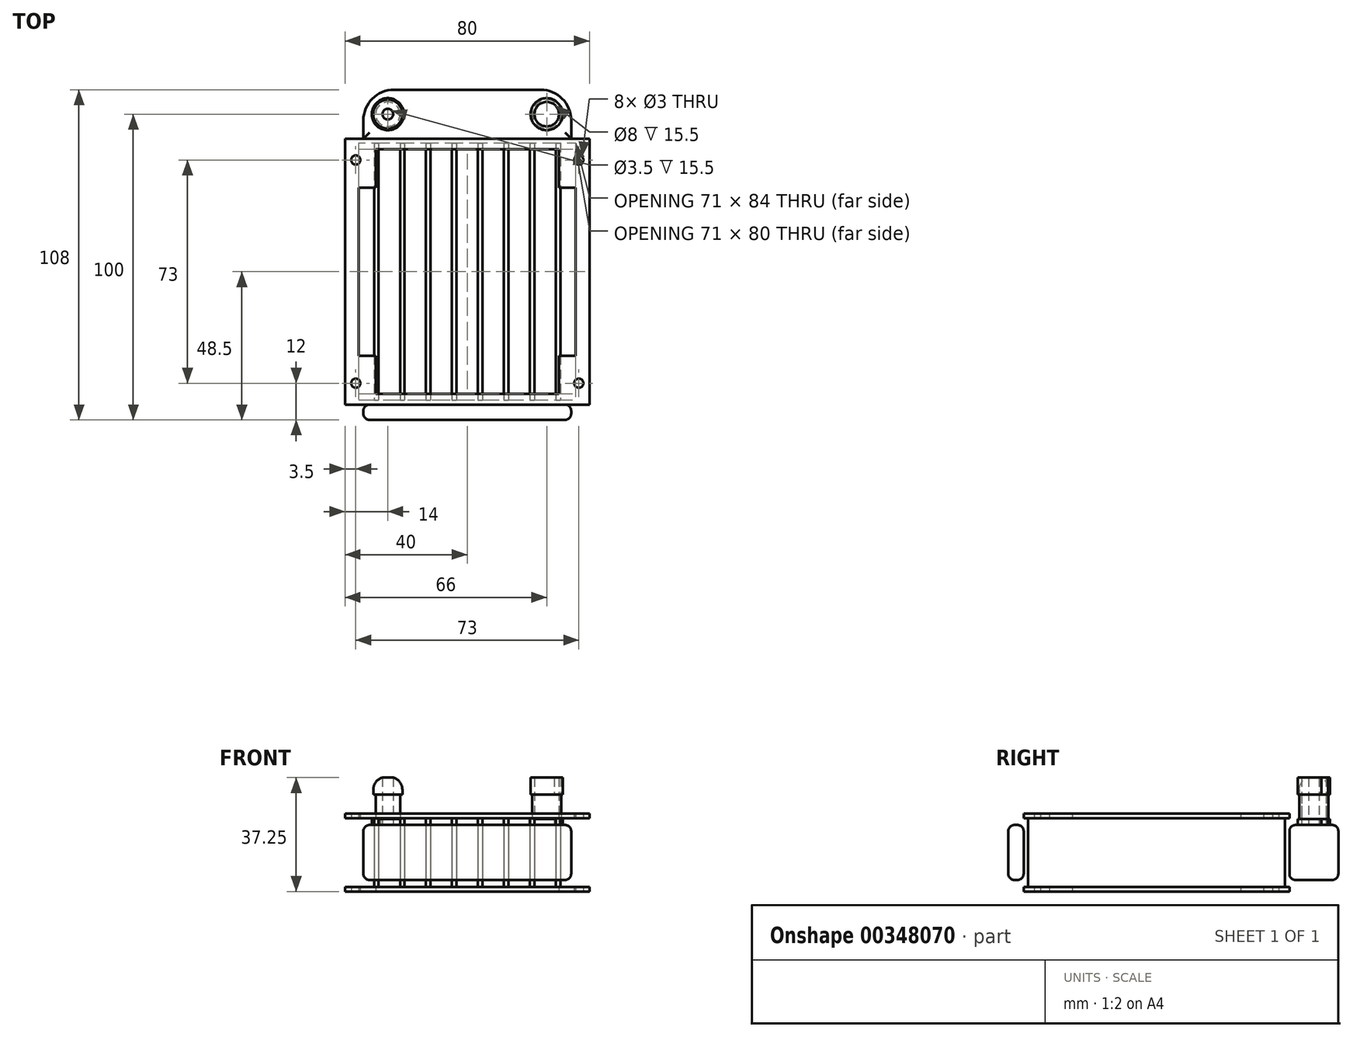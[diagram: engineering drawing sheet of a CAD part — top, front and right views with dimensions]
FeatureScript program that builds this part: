
annotation { "Feature Type Name" : "Feature", "Feature Type Description" : "" }
export const myFeature = defineFeature(function(context is Context, id is Id, definition is map)
    precondition{}
    {
        {
            var Q0;
            Q0=qCreatedBy(makeId("Top.planeOp"),FACE);
            var sketch = newSketch(context, id + "F0", { "sketchPlane" : qUnion([Q0])});
            skLineSegment(sketch, "E0.bottom", {"start": v(-40, 43.5) * mm, "end": v(40, 43.5) * mm});
            skLineSegment(sketch, "E0.top", {"start": v(-40, -43.5) * mm, "end": v(40, -43.5) * mm});
            skLineSegment(sketch, "E0.left", {"start": v(-40, 43.5) * mm, "end": v(-40, -43.5) * mm});
            skLineSegment(sketch, "E0.right", {"start": v(40, 43.5) * mm, "end": v(40, -43.5) * mm});
            skPoint(sketch, "E0.middle", {"position": v(0, 0) * mm});
            skLineSegment(sketch, "E1.bottom", {"start": v(40, 43.5) * mm, "end": v(30, 43.5) * mm});
            skLineSegment(sketch, "E1.top", {"start": v(35.5, 27.5) * mm, "end": v(30, 27.5) * mm});
            skLineSegment(sketch, "E1.left", {"start": v(40, 43.5) * mm, "end": v(40, 27.5) * mm});
            skLineSegment(sketch, "E1.right", {"start": v(30, 40) * mm, "end": v(30, 27.5) * mm});
            skCircle(sketch, "E2", {"center": v(36.5, 36.5) * mm, "radius": 1.5 * mm});
            skLineSegment(sketch, "E3.MirrorCS", {"start": v(-35.5, 27.5) * mm, "end": v(-30, 27.5) * mm});
            skLineSegment(sketch, "E4.MirrorCS", {"start": v(-30, 40) * mm, "end": v(-30, 27.5) * mm});
            skCircle(sketch, "E5.MirrorC", {"center": v(-36.5, 36.5) * mm, "radius": 1.5 * mm});
            skLineSegment(sketch, "E6.MirrorCS", {"start": v(-35.5, -27.5) * mm, "end": v(-30, -27.5) * mm});
            skLineSegment(sketch, "E7.MirrorCS", {"start": v(-30, -40) * mm, "end": v(-30, -27.5) * mm});
            skLineSegment(sketch, "E8.MirrorCS", {"start": v(35.5, -27.5) * mm, "end": v(30, -27.5) * mm});
            skLineSegment(sketch, "E9.MirrorCS", {"start": v(30, -40) * mm, "end": v(30, -27.5) * mm});
            skCircle(sketch, "E10.MirrorC", {"center": v(36.5, -36.5) * mm, "radius": 1.5 * mm});
            skCircle(sketch, "E11.MirrorC", {"center": v(-36.5, -36.5) * mm, "radius": 1.5 * mm});
            skLineSegment(sketch, "E12", {"start": v(35.5, 27.5) * mm, "end": v(35.5, -27.5) * mm});
            skLineSegment(sketch, "E13.MirrorCS", {"start": v(-35.5, 27.5) * mm, "end": v(-35.5, -27.5) * mm});
            skLineSegment(sketch, "E14", {"start": v(-30, 40) * mm, "end": v(30, 40) * mm});
            skLineSegment(sketch, "E15.MirrorCS", {"start": v(-30, -40) * mm, "end": v(30, -40) * mm});
            skPoint(sketch, "E16.orphan", {"position": v(-40, 27.5) * mm});
            skPoint(sketch, "E17.orphan", {"position": v(-40, -27.5) * mm});
            skPoint(sketch, "E18.orphan", {"position": v(40, -27.5) * mm});
            skPoint(sketch, "E19.orphan", {"position": v(-30, -43.5) * mm});
            skPoint(sketch, "E20.orphan", {"position": v(30, -43.5) * mm});
            skPoint(sketch, "E21.orphan", {"position": v(-30, 43.5) * mm});
            skSolve(sketch);
        }
        {
            var Q0;
            Q0=makeQuery(id+"F0.imprint","IMPRINT",FACE,{"disambiguationData":[TD([[makeQuery(id+"F0.imprint","IMPRINT",EDGE,{"derivedFrom":sQuery(id+"F0.wireOp",EDGE,"E0.bottom")}),-1.0]])]});
            extrude(context, id + "F1", {"entities" : qUnion([Q0]), "depth" : 1.5 * mm});
        }
        {
            var Q0;
            Q0=makeQuery(id+"F1.opExtrude","CAP_FACE",FACE,{"disambiguationData":[OSD([sQuery(id+"F0.wireOp",EDGE,"E0.bottom"),sQuery(id+"F0.wireOp",EDGE,"E0.top"),sQuery(id+"F0.wireOp",EDGE,"E0.left"),sQuery(id+"F0.wireOp",EDGE,"E0.right"),sQuery(id+"F0.wireOp",EDGE,"E1.bottom"),sQuery(id+"F0.wireOp",EDGE,"E1.top"),sQuery(id+"F0.wireOp",EDGE,"E1.left"),sQuery(id+"F0.wireOp",EDGE,"E1.right"),sQuery(id+"F0.wireOp",EDGE,"E2"),sQuery(id+"F0.wireOp",EDGE,"E3.MirrorCS"),sQuery(id+"F0.wireOp",EDGE,"E4.MirrorCS"),sQuery(id+"F0.wireOp",EDGE,"E5.MirrorC"),sQuery(id+"F0.wireOp",EDGE,"E6.MirrorCS"),sQuery(id+"F0.wireOp",EDGE,"E7.MirrorCS"),sQuery(id+"F0.wireOp",EDGE,"E8.MirrorCS"),sQuery(id+"F0.wireOp",EDGE,"E9.MirrorCS"),sQuery(id+"F0.wireOp",EDGE,"E10.MirrorC"),sQuery(id+"F0.wireOp",EDGE,"E11.MirrorC"),sQuery(id+"F0.wireOp",EDGE,"E12"),sQuery(id+"F0.wireOp",EDGE,"E13.MirrorCS"),sQuery(id+"F0.wireOp",EDGE,"E14"),sQuery(id+"F0.wireOp",EDGE,"E15.MirrorCS")])],"isStart":false});
            var sketch = newSketch(context, id + "F2", { "sketchPlane" : qUnion([Q0])});
            skLineSegment(sketch, "E22.bottom", {"start": v(-40, 43.5) * mm, "end": v(40, 43.5) * mm});
            skLineSegment(sketch, "E22.top", {"start": v(-40, -43.5) * mm, "end": v(40, -43.5) * mm});
            skLineSegment(sketch, "E22.left", {"start": v(-40, 43.5) * mm, "end": v(-40, -43.5) * mm});
            skLineSegment(sketch, "E22.right", {"start": v(40, 43.5) * mm, "end": v(40, -43.5) * mm});
            skPoint(sketch, "E22.middle", {"position": v(0, 0) * mm});
            skLineSegment(sketch, "E23.bottom", {"start": v(-38.5, 42) * mm, "end": v(38.5, 42) * mm});
            skLineSegment(sketch, "E23.top", {"start": v(-38.5, -42) * mm, "end": v(38.5, -42) * mm});
            skLineSegment(sketch, "E23.left", {"start": v(-38.5, 42) * mm, "end": v(-38.5, -42) * mm});
            skLineSegment(sketch, "E23.right", {"start": v(38.5, 42) * mm, "end": v(38.5, -42) * mm});
            skLineSegment(sketch, "E24.left", {"start": v(-30.5, 42) * mm, "end": v(-30.5, -42) * mm});
            skLineSegment(sketch, "E24.right", {"start": v(-29, 42) * mm, "end": v(-29, -42) * mm});
            skLineSegment(sketch, "E25.1.0.0", {"start": v(-20.5, 42) * mm, "end": v(-20.5, -42) * mm});
            skLineSegment(sketch, "E25.1.0.1", {"start": v(-22, 42) * mm, "end": v(-22, -42) * mm});
            skLineSegment(sketch, "E25.2.0.0", {"start": v(-12, 42) * mm, "end": v(-12, -42) * mm});
            skLineSegment(sketch, "E25.2.0.1", {"start": v(-13.5, 42) * mm, "end": v(-13.5, -42) * mm});
            skLineSegment(sketch, "E25.3.0.0", {"start": v(-3.5, 42) * mm, "end": v(-3.5, -42) * mm});
            skLineSegment(sketch, "E25.3.0.1", {"start": v(-5, 42) * mm, "end": v(-5, -42) * mm});
            skLineSegment(sketch, "E25.4.0.0", {"start": v(5, 42) * mm, "end": v(5, -42) * mm});
            skLineSegment(sketch, "E25.4.0.1", {"start": v(3.5, 42) * mm, "end": v(3.5, -42) * mm});
            skLineSegment(sketch, "E25.5.0.0", {"start": v(13.5, 42) * mm, "end": v(13.5, -42) * mm});
            skLineSegment(sketch, "E25.5.0.1", {"start": v(12, 42) * mm, "end": v(12, -42) * mm});
            skLineSegment(sketch, "E25.6.0.0", {"start": v(22, 42) * mm, "end": v(22, -42) * mm});
            skLineSegment(sketch, "E25.6.0.1", {"start": v(20.5, 42) * mm, "end": v(20.5, -42) * mm});
            skLineSegment(sketch, "E25.7.0.0", {"start": v(30.5, 42) * mm, "end": v(30.5, -42) * mm});
            skLineSegment(sketch, "E25.7.0.1", {"start": v(29, 42) * mm, "end": v(29, -42) * mm});
            skSolve(sketch);
        }
        {
            var Q0;
            Q0=makeQuery(id+"F2.imprint","IMPRINT",FACE,{"disambiguationData":[TD([[makeQuery(id+"F2.imprint","IMPRINT",EDGE,{"derivedFrom":sQuery(id+"F2.wireOp",EDGE,"E22.bottom")}),1.0]])]});
            var Q1;
            {var subQ4=makeQuery(id+"F1.opExtrude","CAP_EDGE",EDGE,{"disambiguationData":[OSD([sQuery(id+"F0.wireOp",EDGE,"E4.MirrorCS")])],"isStart":false});Q1=makeQuery(id+"F2.imprint","IMPRINT",FACE,{"disambiguationData":[TD([[makeQuery(id+"F2.imprint","IMPRINT",EDGE,{"derivedFrom":subQ4}),1.0]])]});}
            var Q2;
            {var subQ5=makeQuery(id+"F1.opExtrude","CAP_EDGE",EDGE,{"disambiguationData":[OSD([sQuery(id+"F0.wireOp",EDGE,"E4.MirrorCS")])],"isStart":false});Q2=makeQuery(id+"F2.imprint","IMPRINT",FACE,{"disambiguationData":[TD([[makeQuery(id+"F2.imprint","IMPRINT",EDGE,{"derivedFrom":subQ5}),-1.0]])]});}
            var Q3;
            {var subQ0=sQuery(id+"F2.wireOp",EDGE,"E25.1.0.0");var subQ1=makeQuery(id+"F1.opExtrude","CAP_EDGE",EDGE,{"disambiguationData":[OSD([sQuery(id+"F0.wireOp",EDGE,"E14")])],"isStart":false});var subQ2=makeQuery(id+"F2.imprint","INTERSECT",VERTEX,{"derivedFrom":[subQ1,subQ0]});Q3=makeQuery(id+"F2.imprint","IMPRINT",FACE,{"disambiguationData":[TD([[makeQuery(id+"F2.imprint","IMPRINT",EDGE,{"disambiguationData":[TD([[subQ2,-1.0]])],"derivedFrom":subQ0}),-1.0]])]});}
            var Q4;
            {var subQ0=sQuery(id+"F2.wireOp",EDGE,"E25.2.0.0");var subQ1=makeQuery(id+"F1.opExtrude","CAP_EDGE",EDGE,{"disambiguationData":[OSD([sQuery(id+"F0.wireOp",EDGE,"E14")])],"isStart":false});var subQ2=makeQuery(id+"F2.imprint","INTERSECT",VERTEX,{"derivedFrom":[subQ1,subQ0]});Q4=makeQuery(id+"F2.imprint","IMPRINT",FACE,{"disambiguationData":[TD([[makeQuery(id+"F2.imprint","IMPRINT",EDGE,{"disambiguationData":[TD([[subQ2,-1.0]])],"derivedFrom":subQ0}),-1.0]])]});}
            var Q5;
            {var subQ0=sQuery(id+"F2.wireOp",EDGE,"E25.3.0.0");var subQ1=makeQuery(id+"F1.opExtrude","CAP_EDGE",EDGE,{"disambiguationData":[OSD([sQuery(id+"F0.wireOp",EDGE,"E14")])],"isStart":false});var subQ2=makeQuery(id+"F2.imprint","INTERSECT",VERTEX,{"derivedFrom":[subQ1,subQ0]});Q5=makeQuery(id+"F2.imprint","IMPRINT",FACE,{"disambiguationData":[TD([[makeQuery(id+"F2.imprint","IMPRINT",EDGE,{"disambiguationData":[TD([[subQ2,-1.0]])],"derivedFrom":subQ0}),-1.0]])]});}
            var Q6;
            {var subQ0=sQuery(id+"F2.wireOp",EDGE,"E25.4.0.0");var subQ1=makeQuery(id+"F1.opExtrude","CAP_EDGE",EDGE,{"disambiguationData":[OSD([sQuery(id+"F0.wireOp",EDGE,"E14")])],"isStart":false});var subQ2=makeQuery(id+"F2.imprint","INTERSECT",VERTEX,{"derivedFrom":[subQ1,subQ0]});Q6=makeQuery(id+"F2.imprint","IMPRINT",FACE,{"disambiguationData":[TD([[makeQuery(id+"F2.imprint","IMPRINT",EDGE,{"disambiguationData":[TD([[subQ2,-1.0]])],"derivedFrom":subQ0}),-1.0]])]});}
            var Q7;
            {var subQ0=sQuery(id+"F2.wireOp",EDGE,"E25.5.0.0");var subQ1=makeQuery(id+"F1.opExtrude","CAP_EDGE",EDGE,{"disambiguationData":[OSD([sQuery(id+"F0.wireOp",EDGE,"E14")])],"isStart":false});var subQ2=makeQuery(id+"F2.imprint","INTERSECT",VERTEX,{"derivedFrom":[subQ1,subQ0]});Q7=makeQuery(id+"F2.imprint","IMPRINT",FACE,{"disambiguationData":[TD([[makeQuery(id+"F2.imprint","IMPRINT",EDGE,{"disambiguationData":[TD([[subQ2,-1.0]])],"derivedFrom":subQ0}),-1.0]])]});}
            var Q8;
            {var subQ0=sQuery(id+"F2.wireOp",EDGE,"E25.6.0.0");var subQ1=makeQuery(id+"F1.opExtrude","CAP_EDGE",EDGE,{"disambiguationData":[OSD([sQuery(id+"F0.wireOp",EDGE,"E14")])],"isStart":false});var subQ2=makeQuery(id+"F2.imprint","INTERSECT",VERTEX,{"derivedFrom":[subQ1,subQ0]});Q8=makeQuery(id+"F2.imprint","IMPRINT",FACE,{"disambiguationData":[TD([[makeQuery(id+"F2.imprint","IMPRINT",EDGE,{"disambiguationData":[TD([[subQ2,-1.0]])],"derivedFrom":subQ0}),-1.0]])]});}
            var Q9;
            {var subQ6=makeQuery(id+"F1.opExtrude","CAP_EDGE",EDGE,{"disambiguationData":[OSD([sQuery(id+"F0.wireOp",EDGE,"E1.right")])],"isStart":false});Q9=makeQuery(id+"F2.imprint","IMPRINT",FACE,{"disambiguationData":[TD([[makeQuery(id+"F2.imprint","IMPRINT",EDGE,{"derivedFrom":subQ6}),-1.0]])]});}
            var Q10;
            {var subQ0=makeQuery(id+"F1.opExtrude","CAP_EDGE",EDGE,{"disambiguationData":[OSD([sQuery(id+"F0.wireOp",EDGE,"E9.MirrorCS")])],"isStart":false});Q10=makeQuery(id+"F2.imprint","IMPRINT",FACE,{"disambiguationData":[TD([[makeQuery(id+"F2.imprint","IMPRINT",EDGE,{"derivedFrom":subQ0}),-1.0]])]});}
            var Q11;
            {var subQ0=makeQuery(id+"F1.opExtrude","CAP_EDGE",EDGE,{"disambiguationData":[OSD([sQuery(id+"F0.wireOp",EDGE,"E1.right")])],"isStart":false});Q11=makeQuery(id+"F2.imprint","IMPRINT",FACE,{"disambiguationData":[TD([[makeQuery(id+"F2.imprint","IMPRINT",EDGE,{"derivedFrom":subQ0}),1.0]])]});}
            var Q12;
            {var subQ5=makeQuery(id+"F1.opExtrude","CAP_EDGE",EDGE,{"disambiguationData":[OSD([sQuery(id+"F0.wireOp",EDGE,"E7.MirrorCS")])],"isStart":false});Q12=makeQuery(id+"F2.imprint","IMPRINT",FACE,{"disambiguationData":[TD([[makeQuery(id+"F2.imprint","IMPRINT",EDGE,{"derivedFrom":subQ5}),1.0]])]});}
            var Q13;
            {var subQ0=sQuery(id+"F2.wireOp",EDGE,"E25.6.0.0");var subQ1=sQuery(id+"F2.wireOp",EDGE,"E23.top");var subQ2=makeQuery(id+"F2.imprint","INTERSECT",VERTEX,{"derivedFrom":[subQ1,subQ0]});Q13=makeQuery(id+"F2.imprint","IMPRINT",FACE,{"disambiguationData":[TD([[makeQuery(id+"F2.imprint","IMPRINT",EDGE,{"disambiguationData":[TD([[subQ2,1.0]])],"derivedFrom":subQ1}),1.0]])]});}
            var Q14;
            {var subQ0=sQuery(id+"F2.wireOp",EDGE,"E25.5.0.0");var subQ1=sQuery(id+"F2.wireOp",EDGE,"E23.top");var subQ2=makeQuery(id+"F2.imprint","INTERSECT",VERTEX,{"derivedFrom":[subQ1,subQ0]});Q14=makeQuery(id+"F2.imprint","IMPRINT",FACE,{"disambiguationData":[TD([[makeQuery(id+"F2.imprint","IMPRINT",EDGE,{"disambiguationData":[TD([[subQ2,1.0]])],"derivedFrom":subQ1}),1.0]])]});}
            var Q15;
            {var subQ0=sQuery(id+"F2.wireOp",EDGE,"E25.3.0.0");var subQ1=sQuery(id+"F2.wireOp",EDGE,"E23.top");var subQ2=makeQuery(id+"F2.imprint","INTERSECT",VERTEX,{"derivedFrom":[subQ1,subQ0]});Q15=makeQuery(id+"F2.imprint","IMPRINT",FACE,{"disambiguationData":[TD([[makeQuery(id+"F2.imprint","IMPRINT",EDGE,{"disambiguationData":[TD([[subQ2,1.0]])],"derivedFrom":subQ1}),1.0]])]});}
            var Q16;
            {var subQ0=sQuery(id+"F2.wireOp",EDGE,"E25.4.0.0");var subQ1=sQuery(id+"F2.wireOp",EDGE,"E23.top");var subQ2=makeQuery(id+"F2.imprint","INTERSECT",VERTEX,{"derivedFrom":[subQ1,subQ0]});Q16=makeQuery(id+"F2.imprint","IMPRINT",FACE,{"disambiguationData":[TD([[makeQuery(id+"F2.imprint","IMPRINT",EDGE,{"disambiguationData":[TD([[subQ2,1.0]])],"derivedFrom":subQ1}),1.0]])]});}
            var Q17;
            {var subQ0=sQuery(id+"F2.wireOp",EDGE,"E25.2.0.0");var subQ1=sQuery(id+"F2.wireOp",EDGE,"E23.top");var subQ2=makeQuery(id+"F2.imprint","INTERSECT",VERTEX,{"derivedFrom":[subQ1,subQ0]});Q17=makeQuery(id+"F2.imprint","IMPRINT",FACE,{"disambiguationData":[TD([[makeQuery(id+"F2.imprint","IMPRINT",EDGE,{"disambiguationData":[TD([[subQ2,1.0]])],"derivedFrom":subQ1}),1.0]])]});}
            var Q18;
            {var subQ0=sQuery(id+"F2.wireOp",EDGE,"E25.1.0.0");var subQ1=sQuery(id+"F2.wireOp",EDGE,"E23.top");var subQ2=makeQuery(id+"F2.imprint","INTERSECT",VERTEX,{"derivedFrom":[subQ1,subQ0]});Q18=makeQuery(id+"F2.imprint","IMPRINT",FACE,{"disambiguationData":[TD([[makeQuery(id+"F2.imprint","IMPRINT",EDGE,{"disambiguationData":[TD([[subQ2,1.0]])],"derivedFrom":subQ1}),1.0]])]});}
            var Q19;
            {var subQ0=sQuery(id+"F2.wireOp",EDGE,"E25.6.0.0");var subQ1=sQuery(id+"F2.wireOp",EDGE,"E23.bottom");var subQ2=makeQuery(id+"F2.imprint","INTERSECT",VERTEX,{"derivedFrom":[subQ1,subQ0]});Q19=makeQuery(id+"F2.imprint","IMPRINT",FACE,{"disambiguationData":[TD([[makeQuery(id+"F2.imprint","IMPRINT",EDGE,{"disambiguationData":[TD([[subQ2,1.0]])],"derivedFrom":subQ1}),-1.0]])]});}
            var Q20;
            {var subQ0=sQuery(id+"F2.wireOp",EDGE,"E25.5.0.0");var subQ1=sQuery(id+"F2.wireOp",EDGE,"E23.bottom");var subQ2=makeQuery(id+"F2.imprint","INTERSECT",VERTEX,{"derivedFrom":[subQ1,subQ0]});Q20=makeQuery(id+"F2.imprint","IMPRINT",FACE,{"disambiguationData":[TD([[makeQuery(id+"F2.imprint","IMPRINT",EDGE,{"disambiguationData":[TD([[subQ2,1.0]])],"derivedFrom":subQ1}),-1.0]])]});}
            var Q21;
            {var subQ0=sQuery(id+"F2.wireOp",EDGE,"E25.4.0.0");var subQ1=sQuery(id+"F2.wireOp",EDGE,"E23.bottom");var subQ2=makeQuery(id+"F2.imprint","INTERSECT",VERTEX,{"derivedFrom":[subQ1,subQ0]});Q21=makeQuery(id+"F2.imprint","IMPRINT",FACE,{"disambiguationData":[TD([[makeQuery(id+"F2.imprint","IMPRINT",EDGE,{"disambiguationData":[TD([[subQ2,1.0]])],"derivedFrom":subQ1}),-1.0]])]});}
            var Q22;
            {var subQ0=sQuery(id+"F2.wireOp",EDGE,"E25.3.0.0");var subQ1=sQuery(id+"F2.wireOp",EDGE,"E23.bottom");var subQ2=makeQuery(id+"F2.imprint","INTERSECT",VERTEX,{"derivedFrom":[subQ1,subQ0]});Q22=makeQuery(id+"F2.imprint","IMPRINT",FACE,{"disambiguationData":[TD([[makeQuery(id+"F2.imprint","IMPRINT",EDGE,{"disambiguationData":[TD([[subQ2,1.0]])],"derivedFrom":subQ1}),-1.0]])]});}
            var Q23;
            {var subQ0=sQuery(id+"F2.wireOp",EDGE,"E25.2.0.0");var subQ1=sQuery(id+"F2.wireOp",EDGE,"E23.bottom");var subQ2=makeQuery(id+"F2.imprint","INTERSECT",VERTEX,{"derivedFrom":[subQ1,subQ0]});Q23=makeQuery(id+"F2.imprint","IMPRINT",FACE,{"disambiguationData":[TD([[makeQuery(id+"F2.imprint","IMPRINT",EDGE,{"disambiguationData":[TD([[subQ2,1.0]])],"derivedFrom":subQ1}),-1.0]])]});}
            var Q24;
            {var subQ0=sQuery(id+"F2.wireOp",EDGE,"E25.1.0.0");var subQ1=sQuery(id+"F2.wireOp",EDGE,"E23.bottom");var subQ2=makeQuery(id+"F2.imprint","INTERSECT",VERTEX,{"derivedFrom":[subQ1,subQ0]});Q24=makeQuery(id+"F2.imprint","IMPRINT",FACE,{"disambiguationData":[TD([[makeQuery(id+"F2.imprint","IMPRINT",EDGE,{"disambiguationData":[TD([[subQ2,1.0]])],"derivedFrom":subQ1}),-1.0]])]});}
            extrude(context, id + "F3", {"entities" : qUnion([Q0, Q1, Q2, Q3, Q4, Q5, Q6, Q7, Q8, Q9, Q10, Q11, Q12, Q13, Q14, Q15, Q16, Q17, Q18, Q19, Q20, Q21, Q22, Q23, Q24]), "operationType" : NewBodyOperationType.ADD, "depth" : (25.5 - 3) * mm});
        }
        {
            var Q0;
            Q0=makeQuery(id+"F0.imprint","IMPRINT",FACE,{"disambiguationData":[TD([[makeQuery(id+"F0.imprint","IMPRINT",EDGE,{"derivedFrom":sQuery(id+"F0.wireOp",EDGE,"E0.bottom")}),-1.0]])]});
            extrude(context, id + "F4", {"entities" : qUnion([Q0]), "operationType" : NewBodyOperationType.ADD, "depth" : 25.5 * mm, "hasSecondDirection" : true, "secondDirectionOppositeDirection" : false, "secondDirectionDepth" : 24 * mm});
        }
        {
            var Q0;
            Q0=makeQuery(id+"F3.boolean.opBoolean","MERGE",FACE,{"derivedFrom":[makeQuery(id+"F1.opExtrude","SWEPT_FACE",FACE,{"disambiguationData":[OSD([sQuery(id+"F0.wireOp",EDGE,"E0.bottom"),sQuery(id+"F0.wireOp",EDGE,"E1.bottom")])]}),makeQuery(id+"F3.opExtrude","SWEPT_FACE",FACE,{"disambiguationData":[OSD([sQuery(id+"F2.wireOp",EDGE,"E22.bottom")])]})]});
            var sketch = newSketch(context, id + "F5", { "sketchPlane" : qUnion([Q0])});
            skLineSegment(sketch, "E26.bottom", {"start": v(-34, 21.75) * mm, "end": v(34, 21.75) * mm});
            skLineSegment(sketch, "E26.top", {"start": v(-34, 3.75) * mm, "end": v(34, 3.75) * mm});
            skLineSegment(sketch, "E26.left", {"start": v(-34, 21.75) * mm, "end": v(-34, 3.75) * mm});
            skLineSegment(sketch, "E26.right", {"start": v(34, 21.75) * mm, "end": v(34, 3.75) * mm});
            skPoint(sketch, "E26.middle", {"position": v(0, 12.75) * mm});
            skLineSegment(sketch, "E27", {"start": v(0, 21.75) * mm, "end": v(0, 25.5) * mm, "construction": true});
            skLineSegment(sketch, "E28", {"start": v(0, 0) * mm, "end": v(0, 3.75) * mm, "construction": true});
            skSolve(sketch);
        }
        {
            var Q0;
            Q0=makeQuery(id+"F5.imprint","IMPRINT",FACE,{"disambiguationData":[TD([[makeQuery(id+"F5.imprint","IMPRINT",EDGE,{"derivedFrom":sQuery(id+"F5.wireOp",EDGE,"E26.bottom")}),-1.0]])]});
            extrude(context, id + "F6", {"entities" : qUnion([Q0]), "operationType" : NewBodyOperationType.ADD, "oppositeDirection" : true, "depth" : (87 + 5) * mm, "hasSecondDirection" : true, "secondDirectionOppositeDirection" : true, "secondDirectionDepth" : 87 * mm});
        }
        {
            var Q0;
            Q0=makeQuery(id+"F5.imprint","IMPRINT",FACE,{"disambiguationData":[TD([[makeQuery(id+"F5.imprint","IMPRINT",EDGE,{"derivedFrom":sQuery(id+"F5.wireOp",EDGE,"E26.bottom")}),-1.0]])]});
            extrude(context, id + "F7", {"entities" : qUnion([Q0]), "operationType" : NewBodyOperationType.ADD, "depth" : 16 * mm});
        }
        {
            var Q0;
            Q0=makeQuery(id+"F7.opExtrude","CAP_EDGE",EDGE,{"disambiguationData":[OSD([sQuery(id+"F5.wireOp",EDGE,"E26.left")])],"isStart":false});
            var Q1;
            Q1=makeQuery(id+"F7.opExtrude","CAP_EDGE",EDGE,{"disambiguationData":[OSD([sQuery(id+"F5.wireOp",EDGE,"E26.right")])],"isStart":false});
            fillet(context, id + "F8", {"entities" : qUnion([Q0, Q1]), "radius" : 10 * mm, "tangentPropagation" : true, "allowEdgeOverflow" : false});
        }
        {
            var Q0;
            Q0=makeQuery(id+"F7.opExtrude","SWEPT_FACE",FACE,{"disambiguationData":[OSD([sQuery(id+"F5.wireOp",EDGE,"E26.top")])]});
            var Q1;
            Q1=makeQuery(id+"F7.opExtrude","SWEPT_FACE",FACE,{"disambiguationData":[OSD([sQuery(id+"F5.wireOp",EDGE,"E26.bottom")])]});
            var Q2;
            Q2=makeQuery(id+"F6.opExtrude","CAP_FACE",FACE,{"disambiguationData":[OSD([sQuery(id+"F5.wireOp",EDGE,"E26.bottom"),sQuery(id+"F5.wireOp",EDGE,"E26.top"),sQuery(id+"F5.wireOp",EDGE,"E26.left"),sQuery(id+"F5.wireOp",EDGE,"E26.right")])],"isStart":false});
            var Q3;
            Q3=makeQuery(id+"F6.opExtrude","CAP_EDGE",EDGE,{"disambiguationData":[OSD([sQuery(id+"F5.wireOp",EDGE,"E26.bottom")])],"isStart":true});
            var Q4;
            Q4=makeQuery(id+"F6.opExtrude","CAP_EDGE",EDGE,{"disambiguationData":[OSD([sQuery(id+"F5.wireOp",EDGE,"E26.left")])],"isStart":true});
            var Q5;
            Q5=makeQuery(id+"F6.opExtrude","CAP_EDGE",EDGE,{"disambiguationData":[OSD([sQuery(id+"F5.wireOp",EDGE,"E26.top")])],"isStart":true});
            var Q6;
            Q6=makeQuery(id+"F6.opExtrude","CAP_EDGE",EDGE,{"disambiguationData":[OSD([sQuery(id+"F5.wireOp",EDGE,"E26.right")])],"isStart":true});
            var Q7;
            Q7=makeQuery(id+"F6.opExtrude","SWEPT_EDGE",EDGE,{"disambiguationData":[OSD([sQuery(id+"F5.wireOp",EDGE,"E26.bottom"),sQuery(id+"F5.wireOp",EDGE,"E26.right")])]});
            var Q8;
            Q8=makeQuery(id+"F6.opExtrude","SWEPT_EDGE",EDGE,{"disambiguationData":[OSD([sQuery(id+"F5.wireOp",EDGE,"E26.top"),sQuery(id+"F5.wireOp",EDGE,"E26.right")])]});
            var Q9;
            Q9=makeQuery(id+"F6.opExtrude","SWEPT_EDGE",EDGE,{"disambiguationData":[OSD([sQuery(id+"F5.wireOp",EDGE,"E26.top"),sQuery(id+"F5.wireOp",EDGE,"E26.left")])]});
            var Q10;
            Q10=makeQuery(id+"F6.opExtrude","SWEPT_EDGE",EDGE,{"disambiguationData":[OSD([sQuery(id+"F5.wireOp",EDGE,"E26.bottom"),sQuery(id+"F5.wireOp",EDGE,"E26.left")])]});
            fillet(context, id + "F9", {"entities" : qUnion([Q0, Q1, Q2, Q3, Q4, Q5, Q6, Q7, Q8, Q9, Q10]), "radius" : 2 * mm, "tangentPropagation" : true, "allowEdgeOverflow" : false});
        }
        {
            var Q0;
            Q0=makeQuery(id+"F7.opExtrude","SWEPT_FACE",FACE,{"disambiguationData":[OSD([sQuery(id+"F5.wireOp",EDGE,"E26.bottom")])]});
            var sketch = newSketch(context, id + "F10", { "sketchPlane" : qUnion([Q0])});
            skCircle(sketch, "E29", {"center": v(-26, 51.5) * mm, "radius": 5.25 * mm});
            skCircle(sketch, "E30.MirrorC", {"center": v(26, 51.5) * mm, "radius": 5.25 * mm});
            skCircle(sketch, "E31", {"center": v(-26, 51.5) * mm, "radius": 4 * mm});
            skCircle(sketch, "E32", {"center": v(-26, 51.5) * mm, "radius": 1.75 * mm});
            skCircle(sketch, "E33", {"center": v(-26, 51.5) * mm, "radius": 4.75 * mm});
            skCircle(sketch, "E34.MirrorC", {"center": v(26, 51.5) * mm, "radius": 4.75 * mm});
            skCircle(sketch, "E35.MirrorC", {"center": v(26, 51.5) * mm, "radius": 4 * mm});
            skCircle(sketch, "E36.MirrorC", {"center": v(26, 51.5) * mm, "radius": 1.75 * mm});
            skSolve(sketch);
        }
        {
            var Q0;
            Q0=makeQuery(id+"F10.imprint","IMPRINT",FACE,{"disambiguationData":[TD([[makeQuery(id+"F10.imprint","IMPRINT",EDGE,{"derivedFrom":sQuery(id+"F10.wireOp",EDGE,"E33")}),-1.0]])]});
            var Q1;
            Q1=makeQuery(id+"F10.imprint","IMPRINT",FACE,{"disambiguationData":[TD([[makeQuery(id+"F10.imprint","IMPRINT",EDGE,{"derivedFrom":sQuery(id+"F10.wireOp",EDGE,"E31")}),-1.0]])]});
            var Q2;
            Q2=makeQuery(id+"F10.imprint","IMPRINT",FACE,{"disambiguationData":[TD([[makeQuery(id+"F10.imprint","IMPRINT",EDGE,{"derivedFrom":sQuery(id+"F10.wireOp",EDGE,"E34.MirrorC")}),1.0]])]});
            var Q3;
            Q3=makeQuery(id+"F10.imprint","IMPRINT",FACE,{"disambiguationData":[TD([[makeQuery(id+"F10.imprint","IMPRINT",EDGE,{"derivedFrom":sQuery(id+"F10.wireOp",EDGE,"E34.MirrorC")}),-1.0]])]});
            extrude(context, id + "F11", {"entities" : qUnion([Q0, Q1, Q2, Q3]), "operationType" : NewBodyOperationType.ADD, "depth" : 2 * mm});
        }
        {
            var Q0;
            Q0=makeQuery(id+"F10.imprint","IMPRINT",FACE,{"disambiguationData":[TD([[makeQuery(id+"F10.imprint","IMPRINT",EDGE,{"derivedFrom":sQuery(id+"F10.wireOp",EDGE,"E31")}),1.0]])]});
            var Q1;
            Q1=makeQuery(id+"F10.imprint","IMPRINT",FACE,{"disambiguationData":[TD([[makeQuery(id+"F10.imprint","IMPRINT",EDGE,{"derivedFrom":sQuery(id+"F10.wireOp",EDGE,"E35.MirrorC")}),-1.0]])]});
            extrude(context, id + "F12", {"entities" : qUnion([Q0, Q1]), "operationType" : NewBodyOperationType.ADD, "depth" : 10 * mm});
        }
        {
            var Q0;
            Q0=makeQuery(id+"F10.imprint","IMPRINT",FACE,{"disambiguationData":[TD([[makeQuery(id+"F10.imprint","IMPRINT",EDGE,{"derivedFrom":sQuery(id+"F10.wireOp",EDGE,"E31")}),-1.0]])]});
            var Q1;
            Q1=makeQuery(id+"F10.imprint","IMPRINT",FACE,{"disambiguationData":[TD([[makeQuery(id+"F10.imprint","IMPRINT",EDGE,{"derivedFrom":sQuery(id+"F10.wireOp",EDGE,"E31")}),1.0]])]});
            var Q2;
            Q2=makeQuery(id+"F10.imprint","IMPRINT",FACE,{"disambiguationData":[TD([[makeQuery(id+"F10.imprint","IMPRINT",EDGE,{"derivedFrom":sQuery(id+"F10.wireOp",EDGE,"E35.MirrorC")}),-1.0]])]});
            var Q3;
            Q3=makeQuery(id+"F10.imprint","IMPRINT",FACE,{"disambiguationData":[TD([[makeQuery(id+"F10.imprint","IMPRINT",EDGE,{"derivedFrom":sQuery(id+"F10.wireOp",EDGE,"E34.MirrorC")}),-1.0]])]});
            extrude(context, id + "F13", {"entities" : qUnion([Q0, Q1, Q2, Q3]), "operationType" : NewBodyOperationType.ADD, "depth" : 15.5 * mm, "hasSecondDirection" : true, "secondDirectionOppositeDirection" : false, "secondDirectionDepth" : 10 * mm});
        }
        {
            var Q0;
            Q0=makeQuery(id+"F13.opExtrude","CAP_EDGE",EDGE,{"disambiguationData":[OSD([sQuery(id+"F10.wireOp",EDGE,"E33")])],"isStart":false});
            var Q1;
            Q1=makeQuery(id+"F13.opExtrude","CAP_EDGE",EDGE,{"disambiguationData":[OSD([sQuery(id+"F10.wireOp",EDGE,"E34.MirrorC")])],"isStart":false});
            fillet(context, id + "F14", {"entities" : qUnion([Q0, Q1]), "radius" : 4 * mm, "tangentPropagation" : true, "allowEdgeOverflow" : false});
        }
    });
